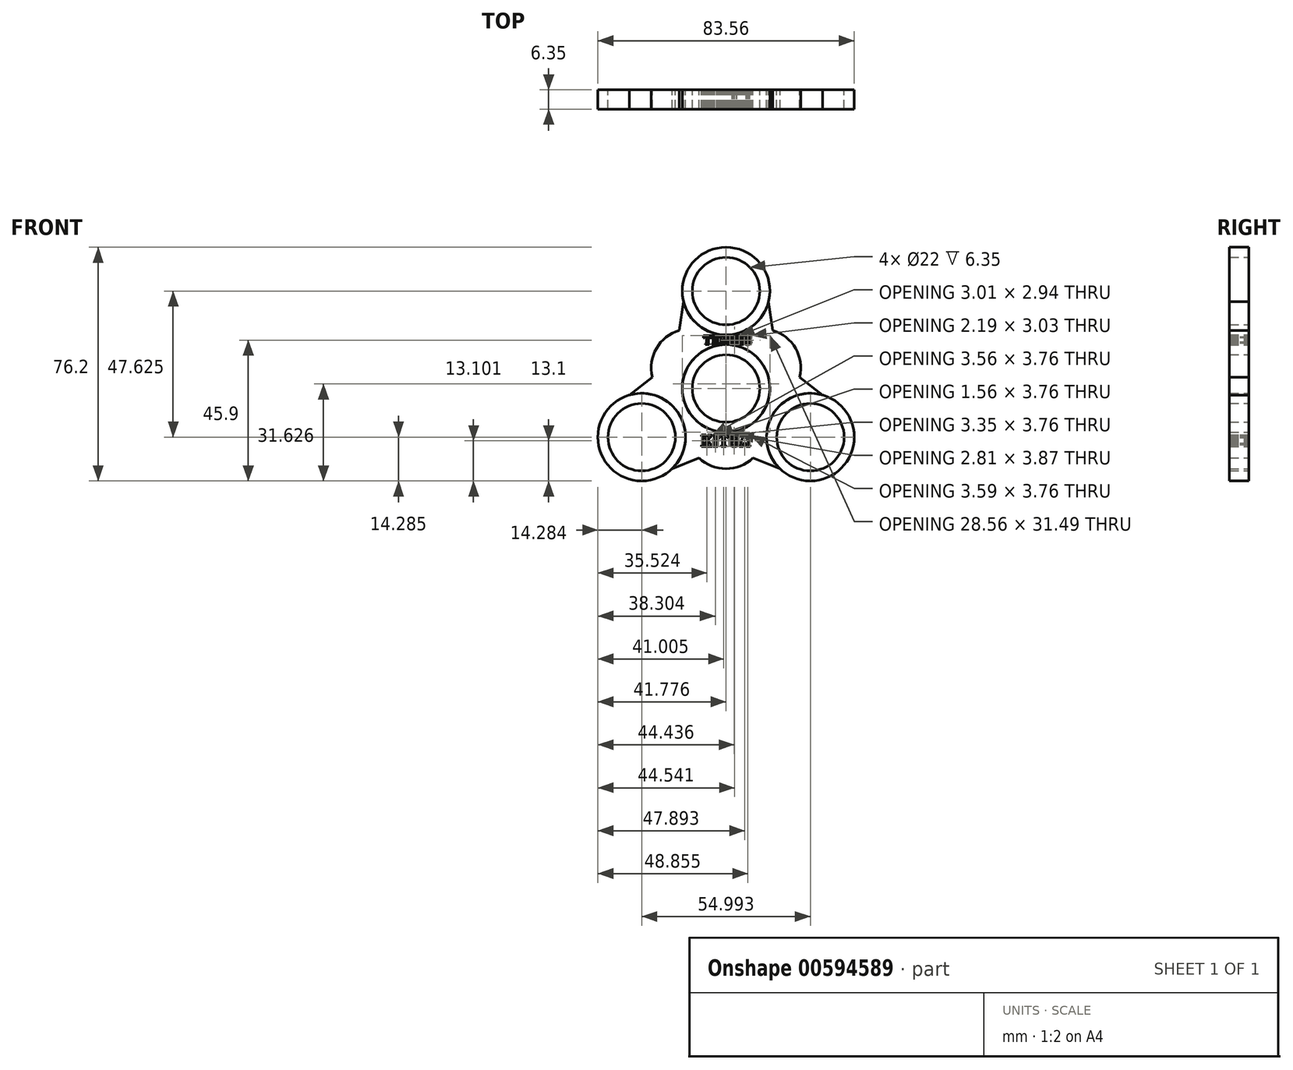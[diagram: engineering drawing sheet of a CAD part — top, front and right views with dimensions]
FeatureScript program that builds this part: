
annotation { "Feature Type Name" : "Feature", "Feature Type Description" : "" }
export const myFeature = defineFeature(function(context is Context, id is Id, definition is map)
    precondition{}
    {
        {
            var Q0;
            Q0=qCreatedBy(makeId("Front.planeOp"),FACE);
            var sketch = newSketch(context, id + "F0", { "sketchPlane" : qUnion([Q0])});
            skCircle(sketch, "E0", {"center": v(0, 0) * mm, "radius": 14.29 * mm});
            skCircle(sketch, "E1", {"center": v(0, 0) * mm, "radius": 11 * mm});
            skCircle(sketch, "E2", {"center": v(0, 31.75) * mm, "radius": 14.29 * mm});
            skCircle(sketch, "E3", {"center": v(0, 31.75) * mm, "radius": 11 * mm});
            skCircle(sketch, "E4.1.0", {"center": v(-27.5, -15.87) * mm, "radius": 14.29 * mm});
            skCircle(sketch, "E4.1.1", {"center": v(-27.5, -15.87) * mm, "radius": 11 * mm});
            skCircle(sketch, "E4.2.0", {"center": v(27.5, -15.88) * mm, "radius": 14.29 * mm});
            skCircle(sketch, "E4.2.1", {"center": v(27.5, -15.88) * mm, "radius": 11 * mm});
            skSolve(sketch);
        }
        {
            var Q0;
            Q0=qCreatedBy(makeId("Front.planeOp"),FACE);
            var sketch = newSketch(context, id + "F1", { "sketchPlane" : qUnion([Q0])});
            skCircle(sketch, "E5.0", {"center": v(0, 31.75) * mm, "radius": 14.29 * mm});
            skCircle(sketch, "E6.0", {"center": v(0, 0) * mm, "radius": 14.29 * mm});
            skCircle(sketch, "E7.0", {"center": v(-27.5, -15.87) * mm, "radius": 14.29 * mm});
            skCircle(sketch, "E8.0", {"center": v(27.5, -15.88) * mm, "radius": 14.29 * mm});
            skArc(sketch, "E9", {"start": v(-31.47, -2.15) * mm, "mid": v(-16.54, 9.55) * mm, "end": v(-13.87, 28.33) * mm});
            skArc(sketch, "E10", {"start": v(13.87, 28.33) * mm, "mid": v(16.54, 9.55) * mm, "end": v(31.47, -2.15) * mm});
            skArc(sketch, "E11", {"start": v(17.6, -26.18) * mm, "mid": v(0, -19.1) * mm, "end": v(-17.6, -26.18) * mm});
            skLineSegment(sketch, "E12", {"start": v(-13.87, 28.33) * mm, "end": v(-16.54, 9.55) * mm});
            skLineSegment(sketch, "E13", {"start": v(-31.47, -2.15) * mm, "end": v(-16.54, 9.55) * mm});
            skArc(sketch, "E14", {"start": v(-15.2, 18.94) * mm, "mid": v(-22.67, 13.09) * mm, "end": v(-24, 3.7) * mm});
            skLineSegment(sketch, "E15.1.0", {"start": v(-17.6, -26.18) * mm, "end": v(0, -19.1) * mm});
            skArc(sketch, "E15.1.1", {"start": v(-8.8, -22.64) * mm, "mid": v(0, -26.18) * mm, "end": v(8.8, -22.64) * mm});
            skLineSegment(sketch, "E15.1.2", {"start": v(17.6, -26.18) * mm, "end": v(0, -19.1) * mm});
            skLineSegment(sketch, "E15.2.0", {"start": v(31.47, -2.15) * mm, "end": v(16.54, 9.55) * mm});
            skArc(sketch, "E15.2.1", {"start": v(24, 3.7) * mm, "mid": v(22.67, 13.09) * mm, "end": v(15.2, 18.94) * mm});
            skLineSegment(sketch, "E15.2.2", {"start": v(13.87, 28.33) * mm, "end": v(16.54, 9.55) * mm});
            skText(sketch, "E16", { "text": "TENNIS", "fontName": "RobotoSlab-Bold.ttf"});
            skText(sketch, "E17", { "text": "KITSA", "fontName": "RobotoSlab-Bold.ttf"});
            const initialGuessF1  = {"E16": [-0.00748, 0.01427, 1, 0, 0.00298], "E17": [-0.00818, -0.01894, 1, 0, 0.00381]};
            skSetInitialGuess(sketch, initialGuessF1);
            skSolve(sketch);
        }
        {
            var Q0;
            Q0=makeQuery(id+"F0.imprint","IMPRINT",FACE,{"disambiguationData":[TD([[makeQuery(id+"F0.imprint","IMPRINT",EDGE,{"derivedFrom":sQuery(id+"F0.wireOp",EDGE,"E2")}),1.0]])]});
            var Q1;
            Q1=makeQuery(id+"F0.imprint","IMPRINT",FACE,{"disambiguationData":[TD([[makeQuery(id+"F0.imprint","IMPRINT",EDGE,{"derivedFrom":sQuery(id+"F0.wireOp",EDGE,"E0")}),1.0]])]});
            var Q2;
            Q2=makeQuery(id+"F0.imprint","IMPRINT",FACE,{"disambiguationData":[TD([[makeQuery(id+"F0.imprint","IMPRINT",EDGE,{"derivedFrom":sQuery(id+"F0.wireOp",EDGE,"E4.2.0")}),1.0]])]});
            var Q3;
            Q3=makeQuery(id+"F0.imprint","IMPRINT",FACE,{"disambiguationData":[TD([[makeQuery(id+"F0.imprint","IMPRINT",EDGE,{"derivedFrom":sQuery(id+"F0.wireOp",EDGE,"E4.1.0")}),1.0]])]});
            var Q4;
            {var subQ3=sQuery(id+"F1.wireOp",EDGE,"E14");Q4=makeQuery(id+"F1.imprint","IMPRINT",FACE,{"disambiguationData":[TD([[makeQuery(id+"F1.imprint","IMPRINT",EDGE,{"derivedFrom":subQ3}),1.0]])]});}
            var Q5;
            {var subQ3=sQuery(id+"F1.wireOp",EDGE,"E15.2.1");Q5=makeQuery(id+"F1.imprint","IMPRINT",FACE,{"disambiguationData":[TD([[makeQuery(id+"F1.imprint","IMPRINT",EDGE,{"derivedFrom":subQ3}),1.0]])]});}
            var Q6;
            {var subQ0=sQuery(id+"F1.wireOp",EDGE,"E15.2.0");var subQ4=makeQuery(id+"F1.imprint","INTERSECT",VERTEX,{"derivedFrom":[subQ0,sQuery(id+"F1.wireOp",EDGE,"E15.2.1")]});Q6=makeQuery(id+"F1.imprint","IMPRINT",FACE,{"disambiguationData":[TD([[makeQuery(id+"F1.imprint","IMPRINT",EDGE,{"disambiguationData":[TD([[subQ4,1.0]])],"derivedFrom":subQ0}),1.0]])]});}
            var Q7;
            {var subQ0=sQuery(id+"F1.wireOp",EDGE,"E15.2.2");var subQ4=makeQuery(id+"F1.imprint","INTERSECT",VERTEX,{"derivedFrom":[sQuery(id+"F1.wireOp",EDGE,"E15.2.1"),subQ0]});Q7=makeQuery(id+"F1.imprint","IMPRINT",FACE,{"disambiguationData":[TD([[makeQuery(id+"F1.imprint","IMPRINT",EDGE,{"disambiguationData":[TD([[subQ4,1.0]])],"derivedFrom":subQ0}),-1.0]])]});}
            var Q8;
            {var subQ0=sQuery(id+"F1.wireOp",EDGE,"E12");var subQ4=makeQuery(id+"F1.imprint","INTERSECT",VERTEX,{"derivedFrom":[subQ0,sQuery(id+"F1.wireOp",EDGE,"E14")]});Q8=makeQuery(id+"F1.imprint","IMPRINT",FACE,{"disambiguationData":[TD([[makeQuery(id+"F1.imprint","IMPRINT",EDGE,{"disambiguationData":[TD([[subQ4,1.0]])],"derivedFrom":subQ0}),1.0]])]});}
            var Q9;
            {var subQ0=sQuery(id+"F1.wireOp",EDGE,"E13");var subQ4=makeQuery(id+"F1.imprint","INTERSECT",VERTEX,{"derivedFrom":[subQ0,sQuery(id+"F1.wireOp",EDGE,"E14")]});Q9=makeQuery(id+"F1.imprint","IMPRINT",FACE,{"disambiguationData":[TD([[makeQuery(id+"F1.imprint","IMPRINT",EDGE,{"disambiguationData":[TD([[subQ4,1.0]])],"derivedFrom":subQ0}),-1.0]])]});}
            var Q10;
            {var subQ0=sQuery(id+"F1.wireOp",EDGE,"E15.1.0");var subQ4=makeQuery(id+"F1.imprint","INTERSECT",VERTEX,{"derivedFrom":[subQ0,sQuery(id+"F1.wireOp",EDGE,"E15.1.1")]});Q10=makeQuery(id+"F1.imprint","IMPRINT",FACE,{"disambiguationData":[TD([[makeQuery(id+"F1.imprint","IMPRINT",EDGE,{"disambiguationData":[TD([[subQ4,1.0]])],"derivedFrom":subQ0}),1.0]])]});}
            var Q11;
            {var subQ3=sQuery(id+"F1.wireOp",EDGE,"E15.1.1");Q11=makeQuery(id+"F1.imprint","IMPRINT",FACE,{"disambiguationData":[TD([[makeQuery(id+"F1.imprint","IMPRINT",EDGE,{"derivedFrom":subQ3}),1.0]])]});}
            var Q12;
            {var subQ0=sQuery(id+"F1.wireOp",EDGE,"E15.1.2");var subQ4=makeQuery(id+"F1.imprint","INTERSECT",VERTEX,{"derivedFrom":[sQuery(id+"F1.wireOp",EDGE,"E15.1.1"),subQ0]});Q12=makeQuery(id+"F1.imprint","IMPRINT",FACE,{"disambiguationData":[TD([[makeQuery(id+"F1.imprint","IMPRINT",EDGE,{"disambiguationData":[TD([[subQ4,1.0]])],"derivedFrom":subQ0}),-1.0]])]});}
            var Q13;
            Q13=makeQuery(id+"F1.imprint","IMPRINT",FACE,{"disambiguationData":[TD([[makeQuery(id+"F1.imprint","IMPRINT",EDGE,{"derivedFrom":sQuery(id+"F1.wireOp",EDGE,"E16.sketch_text.stroke-0")}),1.0]])]});
            extrude(context, id + "F2", {"entities" : qUnion([Q0, Q1, Q2, Q3, Q4, Q5, Q6, Q7, Q8, Q9, Q10, Q11, Q12, Q13]), "depth" : 6.35 * mm, "offsetDistance" : 25.4 * mm});
        }
    });
